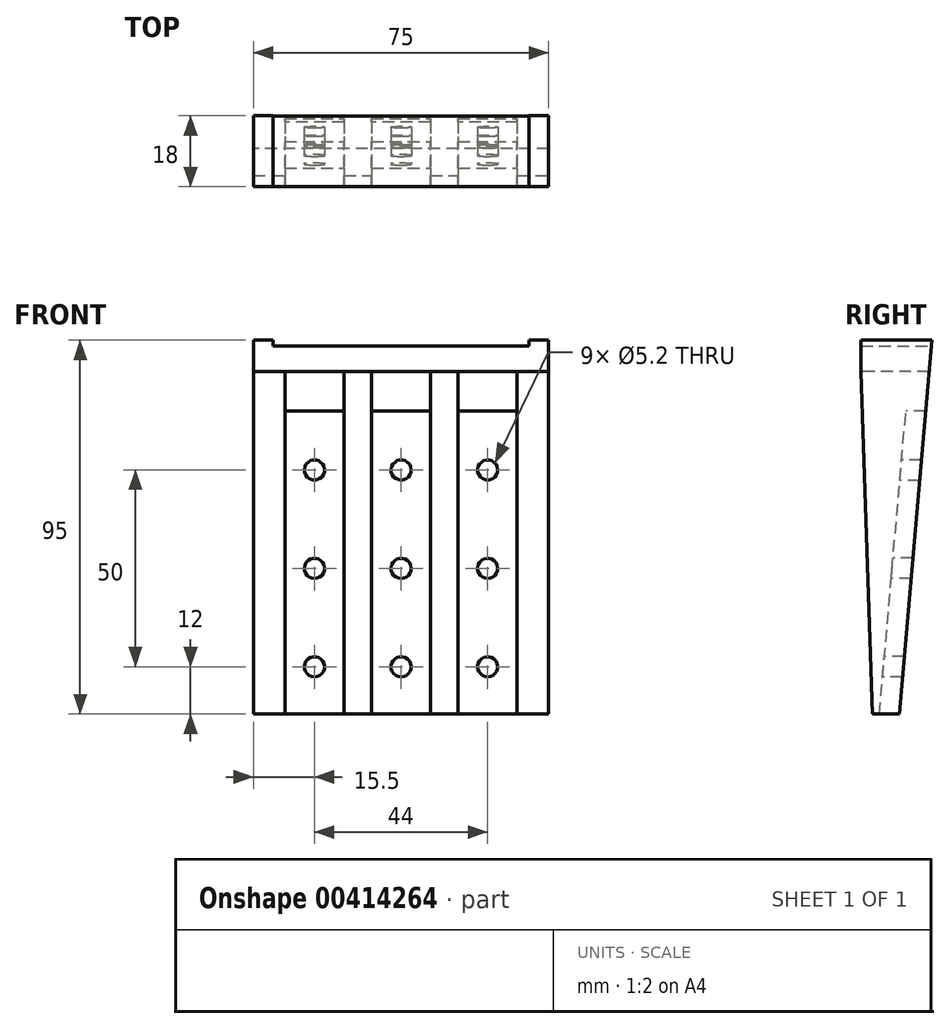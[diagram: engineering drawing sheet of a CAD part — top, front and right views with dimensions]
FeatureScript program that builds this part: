
annotation { "Feature Type Name" : "Feature", "Feature Type Description" : "" }
export const myFeature = defineFeature(function(context is Context, id is Id, definition is map)
    precondition{}
    {
        {
            var Q0;
            Q0=qCreatedBy(makeId("Front.planeOp"),FACE);
            var sketch = newSketch(context, id + "F0", { "sketchPlane" : qUnion([Q0])});
            skLineSegment(sketch, "E0.bottom", {"start": v(0, 0) * mm, "end": v(75, 0) * mm});
            skLineSegment(sketch, "E0.top", {"start": v(0, 100) * mm, "end": v(75, 100) * mm});
            skLineSegment(sketch, "E0.left", {"start": v(0, 0) * mm, "end": v(0, 100) * mm});
            skLineSegment(sketch, "E0.right", {"start": v(75, 0) * mm, "end": v(75, 100) * mm});
            skSolve(sketch);
        }
        {
            var Q0;
            Q0=makeQuery(id+"F0.imprint","IMPRINT",FACE,{"disambiguationData":[TD([[makeQuery(id+"F0.imprint","IMPRINT",EDGE,{"derivedFrom":sQuery(id+"F0.wireOp",EDGE,"E0.bottom")}),1.0]])]});
            extrude(context, id + "F1", {"entities" : qUnion([Q0]), "depth" : 18 * mm});
        }
        {
            var Q0;
            Q0=makeQuery(id+"F1.opExtrude","SWEPT_FACE",FACE,{"disambiguationData":[OSD([sQuery(id+"F0.wireOp",EDGE,"E0.left")])]});
            var sketch = newSketch(context, id + "F2", { "sketchPlane" : qUnion([Q0])});
            skLineSegment(sketch, "E1", {"start": v(15, 0) * mm, "end": v(18, 92) * mm});
            skLineSegment(sketch, "E2", {"start": v(18, 92) * mm, "end": v(18, 0) * mm});
            skLineSegment(sketch, "E3", {"start": v(18, 0) * mm, "end": v(15, 0) * mm});
            skSolve(sketch);
        }
        {
            var Q0;
            Q0=makeQuery(id+"F2.imprint","IMPRINT",FACE,{"disambiguationData":[TD([[makeQuery(id+"F2.imprint","IMPRINT",EDGE,{"derivedFrom":sQuery(id+"F2.wireOp",EDGE,"E1")}),-1.0]])]});
            extrude(context, id + "F3", {"entities" : qUnion([Q0]), "operationType" : NewBodyOperationType.REMOVE, "endBound" : BoundingType.THROUGH_ALL, "oppositeDirection" : true, "depth" : 25 * mm});
        }
        {
            var Q0;
            Q0=makeQuery(id+"F1.opExtrude","CAP_FACE",FACE,{"disambiguationData":[OSD([sQuery(id+"F0.wireOp",EDGE,"E0.bottom"),sQuery(id+"F0.wireOp",EDGE,"E0.top"),sQuery(id+"F0.wireOp",EDGE,"E0.left"),sQuery(id+"F0.wireOp",EDGE,"E0.right")])],"isStart":false});
            var sketch = newSketch(context, id + "F4", { "sketchPlane" : qUnion([Q0])});
            skLineSegment(sketch, "E4.bottom", {"start": v(8, 92) * mm, "end": v(23, 92) * mm});
            skLineSegment(sketch, "E4.top", {"start": v(8, 0) * mm, "end": v(23, 0) * mm});
            skLineSegment(sketch, "E4.left", {"start": v(8, 92) * mm, "end": v(8, 0) * mm});
            skLineSegment(sketch, "E4.right", {"start": v(23, 92) * mm, "end": v(23, 0) * mm});
            skLineSegment(sketch, "E5.bottom", {"start": v(30, 92) * mm, "end": v(45, 92) * mm});
            skLineSegment(sketch, "E5.top", {"start": v(30, 0) * mm, "end": v(45, 0) * mm});
            skLineSegment(sketch, "E5.left", {"start": v(30, 92) * mm, "end": v(30, 0) * mm});
            skLineSegment(sketch, "E5.right", {"start": v(45, 92) * mm, "end": v(45, 0) * mm});
            skLineSegment(sketch, "E6.bottom", {"start": v(52, 92) * mm, "end": v(67, 92) * mm});
            skLineSegment(sketch, "E6.top", {"start": v(52, 0) * mm, "end": v(67, 0) * mm});
            skLineSegment(sketch, "E6.left", {"start": v(52, 92) * mm, "end": v(52, 0) * mm});
            skLineSegment(sketch, "E6.right", {"start": v(67, 92) * mm, "end": v(67, 0) * mm});
            skSolve(sketch);
        }
        {
            var Q0;
            Q0=makeQuery(id+"F4.imprint","IMPRINT",FACE,{"disambiguationData":[TD([[makeQuery(id+"F4.imprint","IMPRINT",EDGE,{"derivedFrom":sQuery(id+"F4.wireOp",EDGE,"E4.bottom")}),1.0]])]});
            var Q1;
            Q1=makeQuery(id+"F4.imprint","IMPRINT",FACE,{"disambiguationData":[TD([[makeQuery(id+"F4.imprint","IMPRINT",EDGE,{"derivedFrom":sQuery(id+"F4.wireOp",EDGE,"E5.bottom")}),1.0]])]});
            var Q2;
            Q2=makeQuery(id+"F4.imprint","IMPRINT",FACE,{"disambiguationData":[TD([[makeQuery(id+"F4.imprint","IMPRINT",EDGE,{"derivedFrom":sQuery(id+"F4.wireOp",EDGE,"E6.bottom")}),1.0]])]});
            extrude(context, id + "F5", {"entities" : qUnion([Q0, Q1, Q2]), "operationType" : NewBodyOperationType.REMOVE, "oppositeDirection" : true, "depth" : 50 * mm});
        }
        {
            var Q0;
            Q0=makeQuery(id+"F1.opExtrude","SWEPT_FACE",FACE,{"disambiguationData":[OSD([sQuery(id+"F0.wireOp",EDGE,"E0.top")])]});
            var sketch = newSketch(context, id + "F6", { "sketchPlane" : qUnion([Q0])});
            skLineSegment(sketch, "E7.bottom", {"start": v(5, -18) * mm, "end": v(70, -18) * mm});
            skLineSegment(sketch, "E7.top", {"start": v(5, 2) * mm, "end": v(70, 2) * mm});
            skLineSegment(sketch, "E7.left", {"start": v(5, -18) * mm, "end": v(5, 2) * mm});
            skLineSegment(sketch, "E7.right", {"start": v(70, -18) * mm, "end": v(70, 2) * mm});
            skSolve(sketch);
        }
        {
            var Q0;
            Q0=makeQuery(id+"F6.imprint","IMPRINT",FACE,{"disambiguationData":[TD([[makeQuery(id+"F6.imprint","IMPRINT",EDGE,{"derivedFrom":sQuery(id+"F6.wireOp",EDGE,"E7.bottom")}),1.0]])]});
            extrude(context, id + "F7", {"entities" : qUnion([Q0]), "operationType" : NewBodyOperationType.REMOVE, "oppositeDirection" : true, "depth" : 1.5 * mm});
        }
        {
            var Q0;
            Q0=makeQuery(id+"F1.opExtrude","SWEPT_FACE",FACE,{"disambiguationData":[OSD([sQuery(id+"F0.wireOp",EDGE,"E0.left")])]});
            var sketch = newSketch(context, id + "F8", { "sketchPlane" : qUnion([Q0])});
            skLineSegment(sketch, "E8", {"start": v(0, 100) * mm, "end": v(8.75, 0) * mm});
            skLineSegment(sketch, "E9", {"start": v(8.75, 0) * mm, "end": v(0, 0) * mm});
            skLineSegment(sketch, "E10", {"start": v(0, 0) * mm, "end": v(0, 100) * mm});
            skSolve(sketch);
        }
        {
            var Q0;
            Q0=makeQuery(id+"F8.imprint","IMPRINT",FACE,{"disambiguationData":[TD([[makeQuery(id+"F8.imprint","IMPRINT",EDGE,{"derivedFrom":sQuery(id+"F8.wireOp",EDGE,"E8")}),-1.0]])]});
            extrude(context, id + "F9", {"entities" : qUnion([Q0]), "operationType" : NewBodyOperationType.REMOVE, "endBound" : BoundingType.THROUGH_ALL, "oppositeDirection" : true, "depth" : 25 * mm});
        }
        {
            var Q0;
            Q0=makeQuery(id+"F1.opExtrude","SWEPT_FACE",FACE,{"disambiguationData":[OSD([sQuery(id+"F0.wireOp",EDGE,"E0.left")])]});
            var sketch = newSketch(context, id + "F10", { "sketchPlane" : qUnion([Q0])});
            skLineSegment(sketch, "E11", {"start": v(0, 100) * mm, "end": v(8.75, 0) * mm});
            skLineSegment(sketch, "E12", {"start": v(8.75, 0) * mm, "end": v(13.77, 0) * mm});
            skLineSegment(sketch, "E13", {"start": v(13.77, 0) * mm, "end": v(5.02, 100) * mm});
            skLineSegment(sketch, "E14", {"start": v(5.02, 100) * mm, "end": v(0, 100) * mm});
            skSolve(sketch);
        }
        {
            var Q0;
            Q0=makeQuery(id+"F10.imprint","IMPRINT",FACE,{"disambiguationData":[TD([[makeQuery(id+"F10.imprint","IMPRINT",EDGE,{"derivedFrom":sQuery(id+"F10.wireOp",EDGE,"E11")}),1.0]])]});
            var Q1;
            Q1=makeQuery(id+"F1.opExtrude","SWEPT_FACE",FACE,{"disambiguationData":[OSD([sQuery(id+"F0.wireOp",EDGE,"E0.right")])]});
            extrude(context, id + "F11", {"entities" : qUnion([Q0]), "operationType" : NewBodyOperationType.ADD, "endBound" : BoundingType.UP_TO_SURFACE, "oppositeDirection" : true, "endBoundEntityFace" : qUnion([Q1]), "depth" : 25 * mm});
        }
        {
            var Q0;
            Q0=makeQuery(id+"F1.opExtrude","CAP_FACE",FACE,{"disambiguationData":[OSD([sQuery(id+"F0.wireOp",EDGE,"E0.bottom"),sQuery(id+"F0.wireOp",EDGE,"E0.top"),sQuery(id+"F0.wireOp",EDGE,"E0.left"),sQuery(id+"F0.wireOp",EDGE,"E0.right")])],"isStart":false});
            var sketch = newSketch(context, id + "F12", { "sketchPlane" : qUnion([Q0])});
            skLineSegment(sketch, "E15.bottom", {"start": v(5, 98.5) * mm, "end": v(70, 98.5) * mm});
            skLineSegment(sketch, "E15.top", {"start": v(5, 100) * mm, "end": v(70, 100) * mm});
            skLineSegment(sketch, "E15.left", {"start": v(5, 98.5) * mm, "end": v(5, 100) * mm});
            skLineSegment(sketch, "E15.right", {"start": v(70, 98.5) * mm, "end": v(70, 100) * mm});
            skSolve(sketch);
        }
        {
            var Q0;
            Q0=makeQuery(id+"F12.imprint","IMPRINT",FACE,{"disambiguationData":[TD([[makeQuery(id+"F12.imprint","IMPRINT",EDGE,{"derivedFrom":sQuery(id+"F12.wireOp",EDGE,"E15.bottom")}),1.0]])]});
            extrude(context, id + "F13", {"entities" : qUnion([Q0]), "operationType" : NewBodyOperationType.REMOVE, "endBound" : BoundingType.THROUGH_ALL, "oppositeDirection" : true, "depth" : 25 * mm});
        }
        {
            var Q0;
            Q0=makeQuery(id+"F1.opExtrude","CAP_FACE",FACE,{"disambiguationData":[OSD([sQuery(id+"F0.wireOp",EDGE,"E0.bottom"),sQuery(id+"F0.wireOp",EDGE,"E0.top"),sQuery(id+"F0.wireOp",EDGE,"E0.left"),sQuery(id+"F0.wireOp",EDGE,"E0.right")])],"isStart":false});
            var sketch = newSketch(context, id + "F14", { "sketchPlane" : qUnion([Q0])});
            skLineSegment(sketch, "E16.bottom", {"start": v(8, 92) * mm, "end": v(23, 92) * mm});
            skLineSegment(sketch, "E16.top", {"start": v(8, 82) * mm, "end": v(23, 82) * mm});
            skLineSegment(sketch, "E16.left", {"start": v(8, 92) * mm, "end": v(8, 82) * mm});
            skLineSegment(sketch, "E16.right", {"start": v(23, 92) * mm, "end": v(23, 82) * mm});
            skLineSegment(sketch, "E17.bottom", {"start": v(30, 92) * mm, "end": v(45, 92) * mm});
            skLineSegment(sketch, "E17.top", {"start": v(30, 82) * mm, "end": v(45, 82) * mm});
            skLineSegment(sketch, "E17.left", {"start": v(30, 92) * mm, "end": v(30, 82) * mm});
            skLineSegment(sketch, "E17.right", {"start": v(45, 92) * mm, "end": v(45, 82) * mm});
            skLineSegment(sketch, "E18.bottom", {"start": v(52, 92) * mm, "end": v(67, 92) * mm});
            skLineSegment(sketch, "E18.top", {"start": v(52, 82) * mm, "end": v(67, 82) * mm});
            skLineSegment(sketch, "E18.left", {"start": v(52, 92) * mm, "end": v(52, 82) * mm});
            skLineSegment(sketch, "E18.right", {"start": v(67, 92) * mm, "end": v(67, 82) * mm});
            skLineSegment(sketch, "E19.bottom", {"start": v(0, 0) * mm, "end": v(75.27, 0) * mm});
            skLineSegment(sketch, "E19.top", {"start": v(0, 5) * mm, "end": v(75.27, 5) * mm});
            skLineSegment(sketch, "E19.left", {"start": v(0, 0) * mm, "end": v(0, 5) * mm});
            skLineSegment(sketch, "E19.right", {"start": v(75.27, 0) * mm, "end": v(75.27, 5) * mm});
            skLineSegment(sketch, "E20", {"start": v(15.5, 82) * mm, "end": v(15.5, 5) * mm, "construction": true});
            skLineSegment(sketch, "E21", {"start": v(37.5, 82) * mm, "end": v(37.5, 5) * mm, "construction": true});
            skLineSegment(sketch, "E22", {"start": v(59.5, 82) * mm, "end": v(59.5, 5) * mm, "construction": true});
            skCircle(sketch, "E23", {"center": v(15.5, 67) * mm, "radius": 2.6 * mm});
            skCircle(sketch, "E24", {"center": v(15.5, 42) * mm, "radius": 2.6 * mm});
            skCircle(sketch, "E25", {"center": v(15.5, 17) * mm, "radius": 2.6 * mm});
            skCircle(sketch, "E26", {"center": v(37.5, 17) * mm, "radius": 2.6 * mm});
            skCircle(sketch, "E27", {"center": v(59.5, 17) * mm, "radius": 2.6 * mm});
            skCircle(sketch, "E28", {"center": v(37.5, 42) * mm, "radius": 2.6 * mm});
            skCircle(sketch, "E29", {"center": v(59.5, 42) * mm, "radius": 2.6 * mm});
            skCircle(sketch, "E30", {"center": v(37.5, 67) * mm, "radius": 2.6 * mm});
            skCircle(sketch, "E31", {"center": v(59.5, 67) * mm, "radius": 2.6 * mm});
            skSolve(sketch);
        }
        {
            var Q0;
            Q0=makeQuery(id+"F14.imprint","IMPRINT",FACE,{"disambiguationData":[TD([[makeQuery(id+"F14.imprint","IMPRINT",EDGE,{"derivedFrom":sQuery(id+"F14.wireOp",EDGE,"E16.bottom")}),1.0]])]});
            var Q1;
            Q1=makeQuery(id+"F14.imprint","IMPRINT",FACE,{"disambiguationData":[TD([[makeQuery(id+"F14.imprint","IMPRINT",EDGE,{"derivedFrom":sQuery(id+"F14.wireOp",EDGE,"E17.bottom")}),1.0]])]});
            var Q2;
            Q2=makeQuery(id+"F14.imprint","IMPRINT",FACE,{"disambiguationData":[TD([[makeQuery(id+"F14.imprint","IMPRINT",EDGE,{"derivedFrom":sQuery(id+"F14.wireOp",EDGE,"E18.bottom")}),1.0]])]});
            var Q3;
            Q3=makeQuery(id+"F14.imprint","IMPRINT",FACE,{"disambiguationData":[TD([[makeQuery(id+"F14.imprint","IMPRINT",EDGE,{"derivedFrom":sQuery(id+"F14.wireOp",EDGE,"E19.bottom")}),1.0]])]});
            var Q4;
            Q4=makeQuery(id+"F14.imprint","IMPRINT",FACE,{"disambiguationData":[TD([[makeQuery(id+"F14.imprint","IMPRINT",EDGE,{"derivedFrom":sQuery(id+"F14.wireOp",EDGE,"E23")}),1.0]])]});
            var Q5;
            Q5=makeQuery(id+"F14.imprint","IMPRINT",FACE,{"disambiguationData":[TD([[makeQuery(id+"F14.imprint","IMPRINT",EDGE,{"derivedFrom":sQuery(id+"F14.wireOp",EDGE,"E30")}),1.0]])]});
            var Q6;
            Q6=makeQuery(id+"F14.imprint","IMPRINT",FACE,{"disambiguationData":[TD([[makeQuery(id+"F14.imprint","IMPRINT",EDGE,{"derivedFrom":sQuery(id+"F14.wireOp",EDGE,"E31")}),1.0]])]});
            var Q7;
            Q7=makeQuery(id+"F14.imprint","IMPRINT",FACE,{"disambiguationData":[TD([[makeQuery(id+"F14.imprint","IMPRINT",EDGE,{"derivedFrom":sQuery(id+"F14.wireOp",EDGE,"E29")}),1.0]])]});
            var Q8;
            Q8=makeQuery(id+"F14.imprint","IMPRINT",FACE,{"disambiguationData":[TD([[makeQuery(id+"F14.imprint","IMPRINT",EDGE,{"derivedFrom":sQuery(id+"F14.wireOp",EDGE,"E28")}),1.0]])]});
            var Q9;
            Q9=makeQuery(id+"F14.imprint","IMPRINT",FACE,{"disambiguationData":[TD([[makeQuery(id+"F14.imprint","IMPRINT",EDGE,{"derivedFrom":sQuery(id+"F14.wireOp",EDGE,"E26")}),1.0]])]});
            var Q10;
            Q10=makeQuery(id+"F14.imprint","IMPRINT",FACE,{"disambiguationData":[TD([[makeQuery(id+"F14.imprint","IMPRINT",EDGE,{"derivedFrom":sQuery(id+"F14.wireOp",EDGE,"E27")}),1.0]])]});
            var Q11;
            Q11=makeQuery(id+"F14.imprint","IMPRINT",FACE,{"disambiguationData":[TD([[makeQuery(id+"F14.imprint","IMPRINT",EDGE,{"derivedFrom":sQuery(id+"F14.wireOp",EDGE,"E25")}),1.0]])]});
            var Q12;
            Q12=makeQuery(id+"F14.imprint","IMPRINT",FACE,{"disambiguationData":[TD([[makeQuery(id+"F14.imprint","IMPRINT",EDGE,{"derivedFrom":sQuery(id+"F14.wireOp",EDGE,"E24")}),1.0]])]});
            extrude(context, id + "F15", {"entities" : qUnion([Q0, Q1, Q2, Q3, Q4, Q5, Q6, Q7, Q8, Q9, Q10, Q11, Q12]), "operationType" : NewBodyOperationType.REMOVE, "endBound" : BoundingType.THROUGH_ALL, "oppositeDirection" : true, "depth" : 25 * mm});
        }
    });
